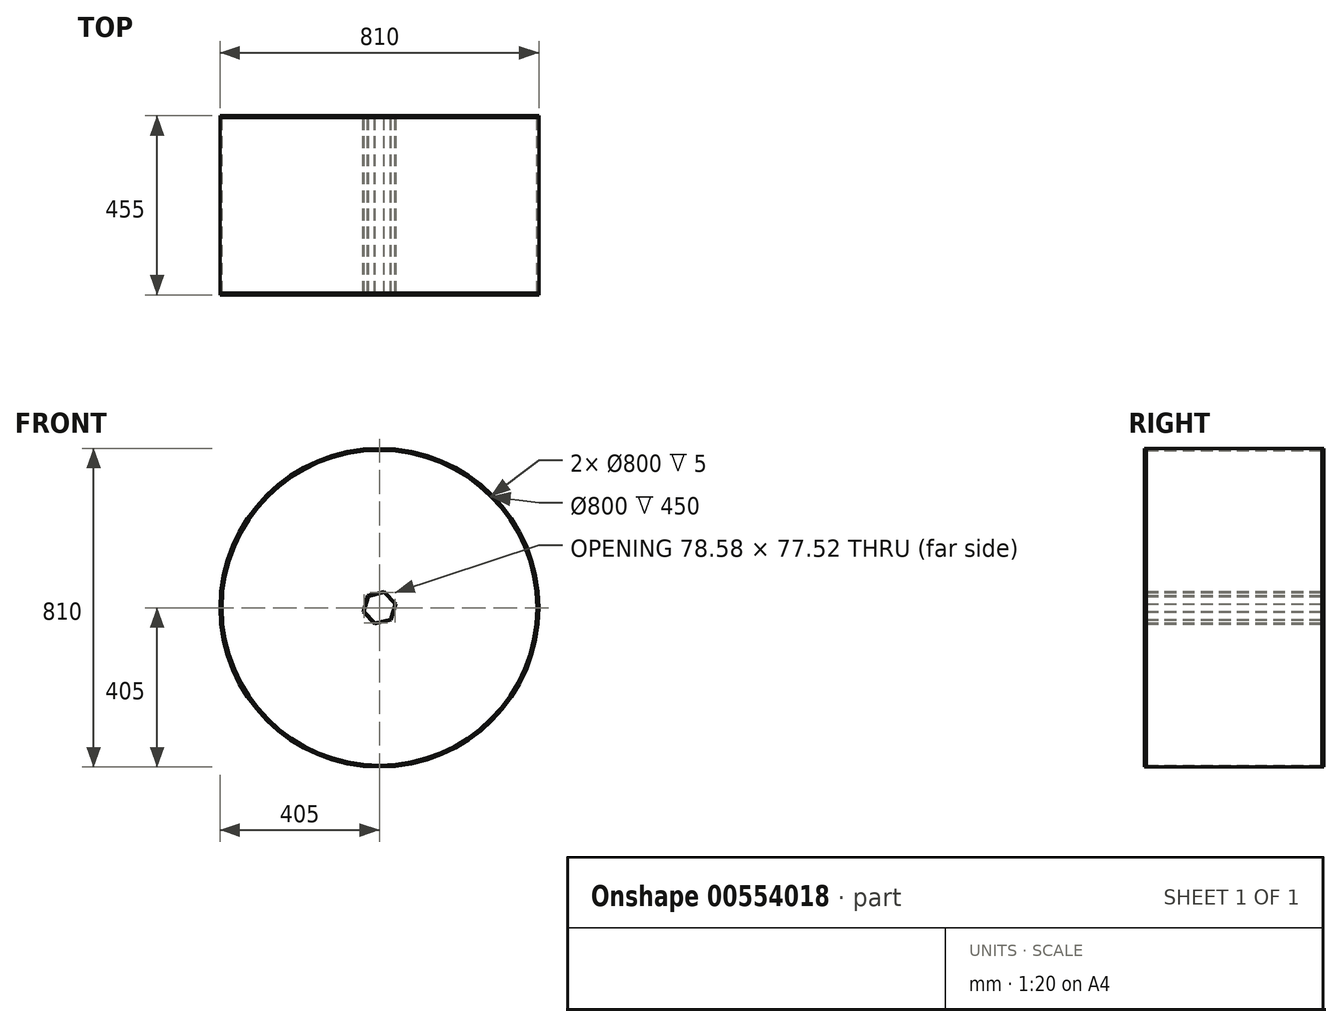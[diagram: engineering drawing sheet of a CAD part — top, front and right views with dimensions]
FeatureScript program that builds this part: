
annotation { "Feature Type Name" : "Feature", "Feature Type Description" : "" }
export const myFeature = defineFeature(function(context is Context, id is Id, definition is map)
    precondition{}
    {
        {
            var Q0;
            Q0=qCreatedBy(makeId("Front.planeOp"),FACE);
            var sketch = newSketch(context, id + "F0", { "sketchPlane" : qUnion([Q0])});
            skCircle(sketch, "E0", {"center": v(0, 0) * mm, "radius": 400 * mm});
            skCircle(sketch, "E1", {"center": v(0, 0) * mm, "radius": 405 * mm});
            skCircle(sketch, "E2.cCircle", {"center": v(0, 0) * mm, "radius": 35 * mm, "construction": true});
            skLineSegment(sketch, "E2.0", {"start": v(27.84, -29.3) * mm, "end": v(-11.45, -38.76) * mm});
            skLineSegment(sketch, "E2.1", {"start": v(-11.45, -38.76) * mm, "end": v(-39.3, -9.47) * mm});
            skLineSegment(sketch, "E2.2", {"start": v(-39.3, -9.47) * mm, "end": v(-27.84, 29.3) * mm});
            skLineSegment(sketch, "E2.3", {"start": v(-27.84, 29.3) * mm, "end": v(11.45, 38.76) * mm});
            skLineSegment(sketch, "E2.4", {"start": v(11.45, 38.76) * mm, "end": v(39.3, 9.47) * mm});
            skLineSegment(sketch, "E2.5", {"start": v(39.3, 9.47) * mm, "end": v(27.84, -29.3) * mm});
            skPoint(sketch, "E2.0.midPoint", {"position": v(8.2, -34.03) * mm});
            skCircle(sketch, "E3.cCircle", {"center": v(0, 0) * mm, "radius": 37.5 * mm, "construction": true});
            skLineSegment(sketch, "E3.0", {"start": v(29.83, -31.39) * mm, "end": v(-12.27, -41.53) * mm});
            skLineSegment(sketch, "E3.1", {"start": v(-12.27, -41.53) * mm, "end": v(-42.1, -10.14) * mm});
            skLineSegment(sketch, "E3.2", {"start": v(-42.1, -10.14) * mm, "end": v(-29.83, 31.39) * mm});
            skLineSegment(sketch, "E3.3", {"start": v(-29.83, 31.39) * mm, "end": v(12.27, 41.53) * mm});
            skLineSegment(sketch, "E3.4", {"start": v(12.27, 41.53) * mm, "end": v(42.1, 10.14) * mm});
            skLineSegment(sketch, "E3.5", {"start": v(42.1, 10.14) * mm, "end": v(29.83, -31.39) * mm});
            skPoint(sketch, "E3.0.midPoint", {"position": v(8.78, -36.46) * mm});
            skSolve(sketch);
        }
        {
            var Q0;
            Q0=makeQuery(id+"F0.imprint","IMPRINT",FACE,{"disambiguationData":[TD([[makeQuery(id+"F0.imprint","IMPRINT",EDGE,{"derivedFrom":sQuery(id+"F0.wireOp",EDGE,"E0")}),-1.0]])]});
            var Q1;
            Q1=makeQuery(id+"F0.imprint","IMPRINT",FACE,{"disambiguationData":[TD([[makeQuery(id+"F0.imprint","IMPRINT",EDGE,{"derivedFrom":sQuery(id+"F0.wireOp",EDGE,"E2.0")}),1.0]])]});
            extrude(context, id + "F1", {"entities" : qUnion([Q0, Q1]), "depth" : 450 * mm, "offsetDistance" : 25.4 * mm});
        }
        {
            var Q0;
            Q0=makeQuery(id+"F0.imprint","IMPRINT",FACE,{"disambiguationData":[TD([[makeQuery(id+"F0.imprint","IMPRINT",EDGE,{"derivedFrom":sQuery(id+"F0.wireOp",EDGE,"E0")}),1.0]])]});
            var Q1;
            Q1=makeQuery(id+"F0.imprint","IMPRINT",FACE,{"disambiguationData":[TD([[makeQuery(id+"F0.imprint","IMPRINT",EDGE,{"derivedFrom":sQuery(id+"F0.wireOp",EDGE,"E2.0")}),-1.0]])]});
            var Q2;
            Q2=makeQuery(id+"F0.imprint","IMPRINT",FACE,{"disambiguationData":[TD([[makeQuery(id+"F0.imprint","IMPRINT",EDGE,{"derivedFrom":sQuery(id+"F0.wireOp",EDGE,"E2.0")}),1.0]])]});
            var Q3;
            Q3=makeQuery(id+"F0.imprint","IMPRINT",FACE,{"disambiguationData":[TD([[makeQuery(id+"F0.imprint","IMPRINT",EDGE,{"derivedFrom":sQuery(id+"F0.wireOp",EDGE,"E0")}),-1.0]])]});
            var Q4;
            Q4=makeQuery(id+"F1.opExtrude","CAP_FACE",FACE,{"disambiguationData":[OSD([sQuery(id+"F0.wireOp",EDGE,"E0"),sQuery(id+"F0.wireOp",EDGE,"E1")])],"isStart":false});
            var Q5;
            Q5=makeQuery(id+"F1.opExtrude","CAP_FACE",FACE,{"disambiguationData":[OSD([sQuery(id+"F0.wireOp",EDGE,"E0"),sQuery(id+"F0.wireOp",EDGE,"E1")])],"isStart":true});
            extrude(context, id + "F2", {"entities" : qUnion([Q0, Q1, Q2, Q3, Q4, Q5]), "depth" : 5 * mm, "offsetDistance" : 25.4 * mm});
        }
    });
